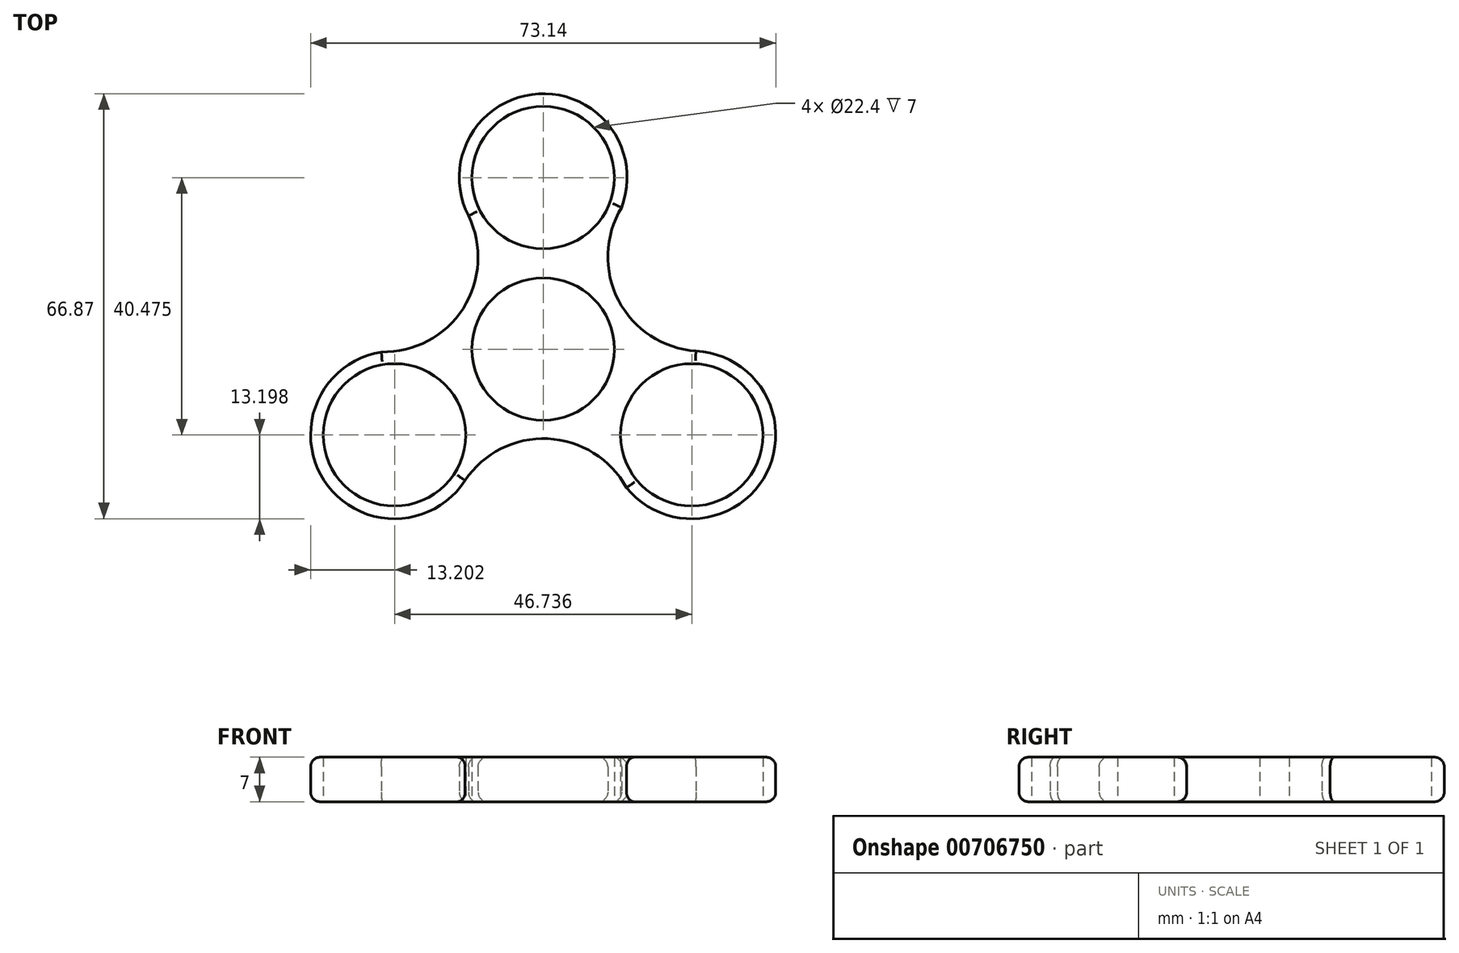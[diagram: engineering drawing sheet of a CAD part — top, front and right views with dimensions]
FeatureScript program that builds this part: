
annotation { "Feature Type Name" : "Feature", "Feature Type Description" : "" }
export const myFeature = defineFeature(function(context is Context, id is Id, definition is map)
    precondition{}
    {
        {
            var Q0;
            Q0=qCreatedBy(makeId("Top.planeOp"),FACE);
            var sketch = newSketch(context, id + "F0", { "sketchPlane" : qUnion([Q0])});
            skCircle(sketch, "E0", {"center": v(0, 0) * mm, "radius": 11.2 * mm});
            skCircle(sketch, "E1", {"center": v(0, 26.98) * mm, "radius": 11.2 * mm});
            skArc(sketch, "E2", {"start": v(11.22, 20.02) * mm, "mid": v(0.54, 40.17) * mm, "end": v(-11.74, 20.96) * mm});
            skCircle(sketch, "E3.1.0", {"center": v(-23.37, -13.5) * mm, "radius": 11.2 * mm});
            skArc(sketch, "E3.1.1", {"start": v(-22.95, -0.3) * mm, "mid": v(-35.06, -19.62) * mm, "end": v(-12.28, -20.65) * mm});
            skCircle(sketch, "E3.2.0", {"center": v(23.37, -13.5) * mm, "radius": 11.2 * mm});
            skArc(sketch, "E3.2.1", {"start": v(11.73, -19.72) * mm, "mid": v(34.52, -20.55) * mm, "end": v(24.02, -0.3) * mm});
            skArc(sketch, "E4", {"start": v(12.32, 22.25) * mm, "mid": v(11.84, 7.68) * mm, "end": v(24.02, -0.3) * mm});
            skArc(sketch, "E5.1.0", {"start": v(-25.43, -0.45) * mm, "mid": v(-12.57, 6.4) * mm, "end": v(-11.74, 20.96) * mm});
            skArc(sketch, "E5.2.0", {"start": v(13.1, -21.8) * mm, "mid": v(0.74, -14.1) * mm, "end": v(-12.28, -20.65) * mm});
            skSolve(sketch);
        }
        {
            var Q0;
            Q0=makeQuery(id+"F0.imprint","IMPRINT",FACE,{"disambiguationData":[TD([[makeQuery(id+"F0.imprint","IMPRINT",EDGE,{"derivedFrom":sQuery(id+"F0.wireOp",EDGE,"E0")}),-1.0]])]});
            extrude(context, id + "F1", {"entities" : qUnion([Q0]), "depth" : 7 * mm, "offsetDistance" : 25 * mm});
        }
        {
            var Q0;
            Q0=makeQuery(id+"F1.opExtrude","CAP_EDGE",EDGE,{"disambiguationData":[OSD([sQuery(id+"F0.wireOp",EDGE,"E3.1.1")])],"isStart":false});
            var Q1;
            Q1=makeQuery(id+"F1.opExtrude","CAP_EDGE",EDGE,{"disambiguationData":[OSD([sQuery(id+"F0.wireOp",EDGE,"E5.2.0")])],"isStart":false});
            var Q2;
            Q2=makeQuery(id+"F1.opExtrude","CAP_EDGE",EDGE,{"disambiguationData":[OSD([sQuery(id+"F0.wireOp",EDGE,"E5.1.0")])],"isStart":false});
            var Q3;
            Q3=makeQuery(id+"F1.opExtrude","CAP_EDGE",EDGE,{"disambiguationData":[OSD([sQuery(id+"F0.wireOp",EDGE,"E2")])],"isStart":false});
            var Q4;
            Q4=makeQuery(id+"F1.opExtrude","CAP_EDGE",EDGE,{"disambiguationData":[OSD([sQuery(id+"F0.wireOp",EDGE,"E4")])],"isStart":false});
            var Q5;
            Q5=makeQuery(id+"F1.opExtrude","CAP_EDGE",EDGE,{"disambiguationData":[OSD([sQuery(id+"F0.wireOp",EDGE,"E3.2.1")])],"isStart":false});
            fillet(context, id + "F2", {"entities" : qUnion([Q0, Q1, Q2, Q3, Q4, Q5]), "radius" : 1.5 * mm, "tangentPropagation" : true, "allowEdgeOverflow" : false});
        }
        {
            var Q0;
            Q0=makeQuery(id+"F1.opExtrude","CAP_EDGE",EDGE,{"disambiguationData":[OSD([sQuery(id+"F0.wireOp",EDGE,"E5.2.0")])],"isStart":true});
            var Q1;
            Q1=makeQuery(id+"F1.opExtrude","CAP_EDGE",EDGE,{"disambiguationData":[OSD([sQuery(id+"F0.wireOp",EDGE,"E3.1.1")])],"isStart":true});
            var Q2;
            Q2=makeQuery(id+"F1.opExtrude","CAP_EDGE",EDGE,{"disambiguationData":[OSD([sQuery(id+"F0.wireOp",EDGE,"E5.1.0")])],"isStart":true});
            var Q3;
            Q3=makeQuery(id+"F1.opExtrude","CAP_EDGE",EDGE,{"disambiguationData":[OSD([sQuery(id+"F0.wireOp",EDGE,"E4")])],"isStart":true});
            var Q4;
            Q4=makeQuery(id+"F1.opExtrude","CAP_EDGE",EDGE,{"disambiguationData":[OSD([sQuery(id+"F0.wireOp",EDGE,"E3.2.1")])],"isStart":true});
            var Q5;
            Q5=makeQuery(id+"F1.opExtrude","CAP_EDGE",EDGE,{"disambiguationData":[OSD([sQuery(id+"F0.wireOp",EDGE,"E2")])],"isStart":true});
            fillet(context, id + "F3", {"entities" : qUnion([Q0, Q1, Q2, Q3, Q4, Q5]), "radius" : 1.5 * mm, "tangentPropagation" : true, "allowEdgeOverflow" : false});
        }
    });
